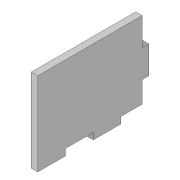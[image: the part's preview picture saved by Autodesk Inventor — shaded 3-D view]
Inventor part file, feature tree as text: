
AUTODESK INVENTOR PART (.ipt)
format: ipt  version: 2017 (Build 210142000, 142)  size: 104,448 bytes
history: native  units: in
note: dims shown in document units (in); Inventor stores cm internally (conversion verified against a paired STEP export)
features: extrude x3, sketch x3
ambient origin geometry x8: Origin, YZ Plane, XZ Plane, XY Plane, X Axis, Y Axis, Z Axis, Center Point
bodies: Solid1 (feature_tree)
feature tree (6):
  extrude  "Extrusion1"  Depth=2.0in
  extrude  "Extrusion2"  Depth=0.5in
  extrude  "Extrusion3"  Depth=0.5in
  sketch  "Sketch1"  dims[d0=1.5in d1=2.0in]
  sketch  "Sketch2"  dims[d2=0.117in d3=0.0in d4=0.5in]
  sketch  "Sketch3"  dims[d5=0.117in d6=0.5in d7=0.117in d8=0.0in d9=0.0in d10=0.0in d11=0.5in d12=0.117in d13=0.7874in d15=1.0in d16=0.3937in d18=1.0in d20=1.0in d21=0.0in]
